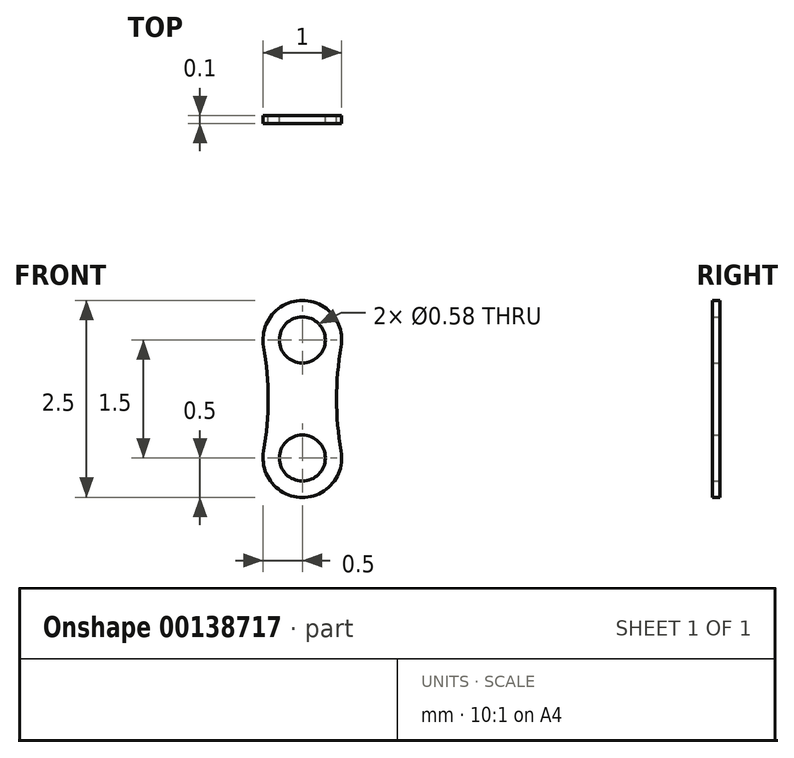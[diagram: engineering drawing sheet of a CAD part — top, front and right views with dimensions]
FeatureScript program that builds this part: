
annotation { "Feature Type Name" : "Feature", "Feature Type Description" : "" }
export const myFeature = defineFeature(function(context is Context, id is Id, definition is map)
    precondition{}
    {
        {
            var Q0;
            Q0=qCreatedBy(makeId("Front.planeOp"),FACE);
            var sketch = newSketch(context, id + "F0", { "sketchPlane" : qUnion([Q0])});
            skCircle(sketch, "E0", {"center": v(0, 0) * mm, "radius": 0.5 * mm});
            skCircle(sketch, "E1", {"center": v(0, -1.5) * mm, "radius": 0.5 * mm});
            skArc(sketch, "E2", {"start": v(-0.5, -1.41) * mm, "mid": v(-0.43, -0.75) * mm, "end": v(-0.5, -0.09) * mm});
            skArc(sketch, "E3", {"start": v(0.5, -0.09) * mm, "mid": v(0.43, -0.75) * mm, "end": v(0.5, -1.41) * mm});
            skCircle(sketch, "E4", {"center": v(0, 0) * mm, "radius": 0.3 * mm});
            skCircle(sketch, "E5", {"center": v(0, -1.5) * mm, "radius": 0.3 * mm});
            skSolve(sketch);
        }
        {
            var Q0;
            Q0 = qSketchRegion(id + "F0", true);
            extrude(context, id + "F1", {"entities" : qUnion([Q0]), "depth" : 0.1 * mm});
        }
    });
